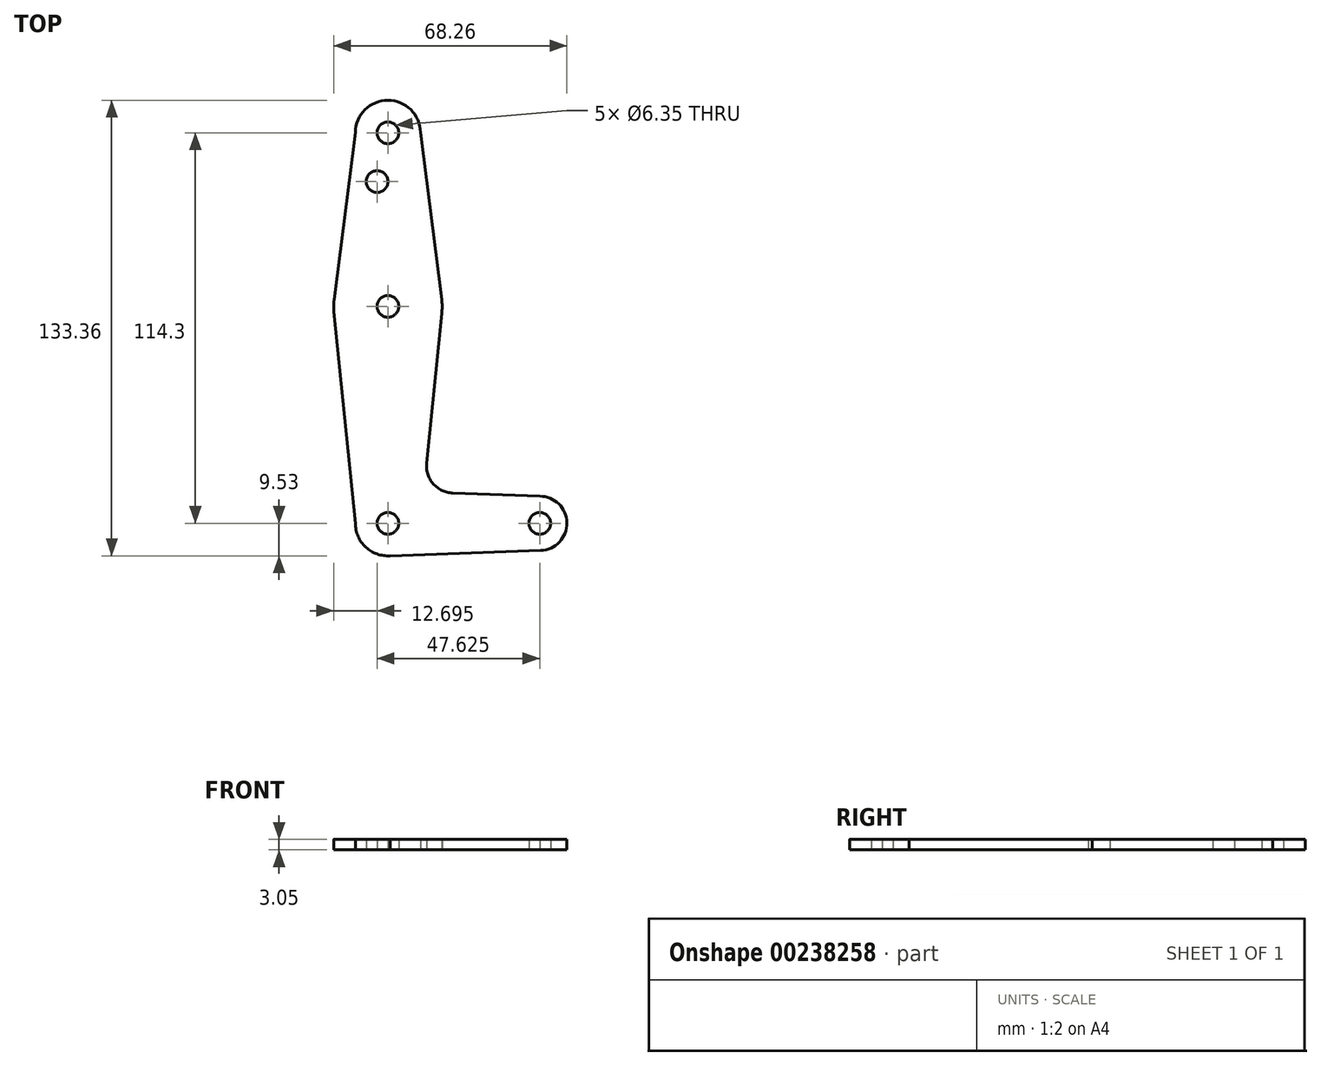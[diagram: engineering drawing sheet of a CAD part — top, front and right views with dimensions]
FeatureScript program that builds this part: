
annotation { "Feature Type Name" : "Feature", "Feature Type Description" : "" }
export const myFeature = defineFeature(function(context is Context, id is Id, definition is map)
    precondition{}
    {
        {
            var Q0;
            Q0=qCreatedBy(makeId("Top.planeOp"),FACE);
            var sketch = newSketch(context, id + "F0", { "sketchPlane" : qUnion([Q0])});
            skCircle(sketch, "E0", {"center": v(0, 0) * mm, "radius": 9.53 * mm});
            skCircle(sketch, "E1", {"center": v(0, 63.5) * mm, "radius": 15.88 * mm});
            skCircle(sketch, "E2", {"center": v(0, 114.3) * mm, "radius": 9.53 * mm});
            skCircle(sketch, "E3", {"center": v(44.45, 0) * mm, "radius": 7.94 * mm});
            skLineSegment(sketch, "E4", {"start": v(0, 0) * mm, "end": v(44.45, 0) * mm});
            skLineSegment(sketch, "E5", {"start": v(0, 114.3) * mm, "end": v(0, 63.5) * mm});
            skLineSegment(sketch, "E6", {"start": v(-9.52, 114.4) * mm, "end": v(-15.75, 65.5) * mm});
            skLineSegment(sketch, "E7", {"start": v(9.52, 114.4) * mm, "end": v(15.75, 65.5) * mm});
            skLineSegment(sketch, "E8", {"start": v(18.97, 8.85) * mm, "end": v(44.45, 7.94) * mm});
            skLineSegment(sketch, "E9", {"start": v(0, -9.52) * mm, "end": v(44.73, -7.93) * mm});
            skCircle(sketch, "E10", {"center": v(0, 114.3) * mm, "radius": 3.18 * mm});
            skCircle(sketch, "E11", {"center": v(0, 63.5) * mm, "radius": 3.18 * mm});
            skCircle(sketch, "E12", {"center": v(0, 0) * mm, "radius": 3.18 * mm});
            skCircle(sketch, "E13", {"center": v(44.45, 0) * mm, "radius": 3.18 * mm});
            skLineSegment(sketch, "E14", {"start": v(15.75, 61.47) * mm, "end": v(11.34, 17.59) * mm});
            skArc(sketch, "E15.filletArc", {"start": v(11.34, 17.59) * mm, "mid": v(13.26, 11.57) * mm, "end": v(18.97, 8.85) * mm});
            skLineSegment(sketch, "E16", {"start": v(0, 63.5) * mm, "end": v(0, 0) * mm});
            skLineSegment(sketch, "E17", {"start": v(-9.53, 0) * mm, "end": v(-15.8, 61.9) * mm});
            skPoint(sketch, "E18", {"position": v(9.53, 0) * mm});
            skPoint(sketch, "E19", {"position": v(0, 9.53) * mm});
            skCircle(sketch, "E20", {"center": v(-3.17, 100.03) * mm, "radius": 3.18 * mm});
            skSolve(sketch);
        }
        {
            var Q0;
            Q0 = qSketchRegion(id + "F0", true);
            extrude(context, id + "F1", {"entities" : qUnion([Q0]), "depth" : 3.05 * mm});
        }
        {
            var Q0;
            {var subQ0=sQuery(id+"F0.wireOp",EDGE,"E16");var subQ1=sQuery(id+"F0.wireOp",EDGE,"E0");var subQ2=makeQuery(id+"F0.imprint","INTERSECT",VERTEX,{"derivedFrom":[subQ1,subQ0]});Q0=makeQuery(id+"F0.imprint","IMPRINT",FACE,{"disambiguationData":[TD([[makeQuery(id+"F0.imprint","IMPRINT",EDGE,{"disambiguationData":[TD([[subQ2,1.0]])],"derivedFrom":subQ1}),1.0]])]});}
            extrude(context, id + "F2", {"entities" : qUnion([Q0]), "operationType" : NewBodyOperationType.ADD, "depth" : 3.05 * mm});
        }
    });
